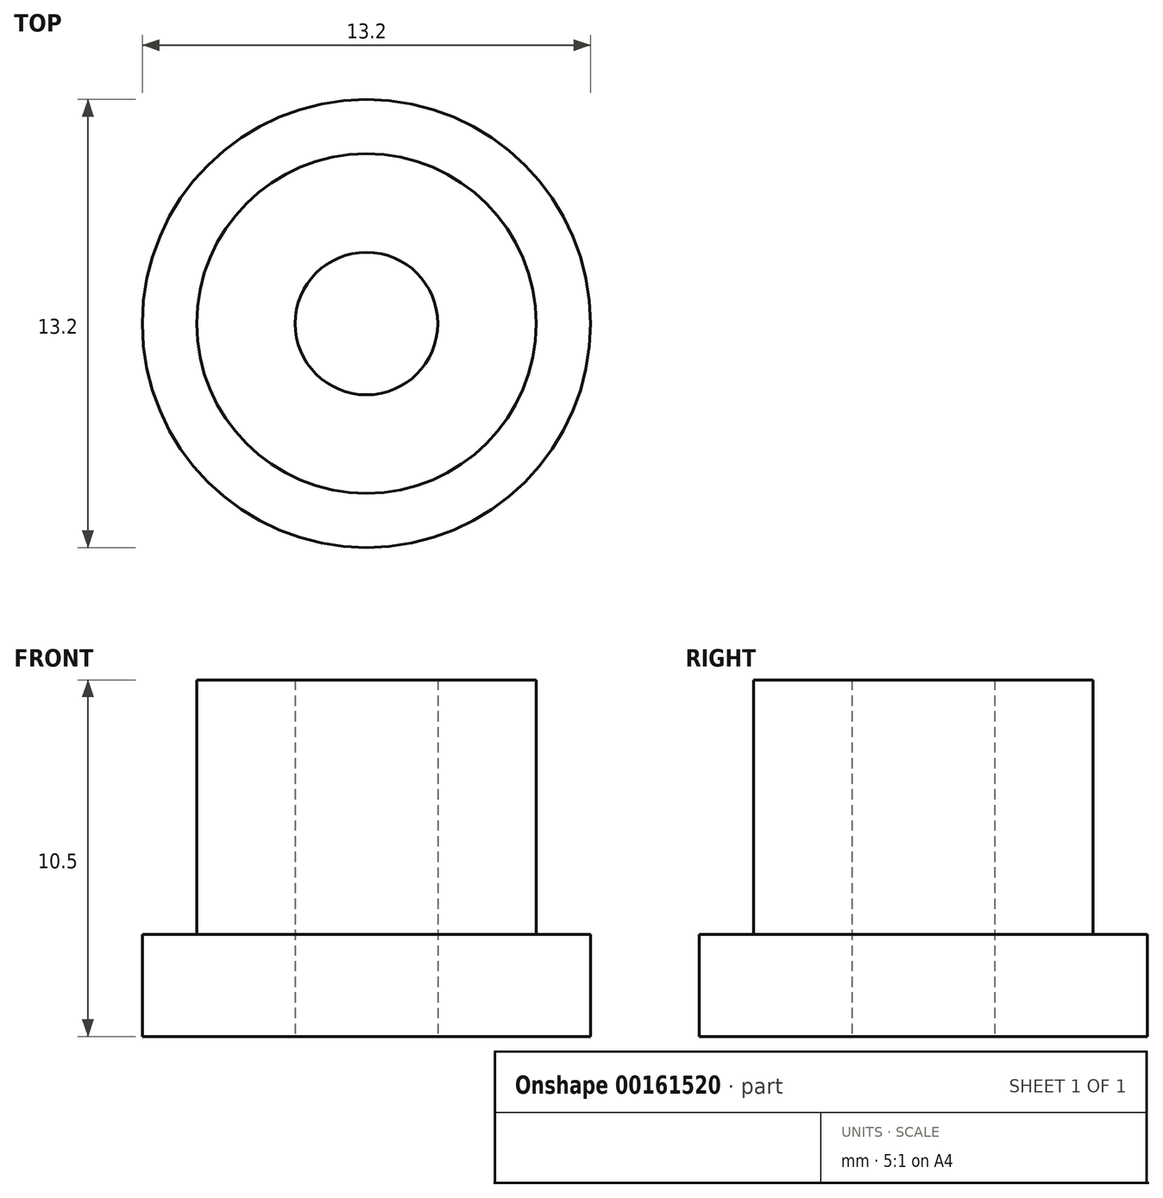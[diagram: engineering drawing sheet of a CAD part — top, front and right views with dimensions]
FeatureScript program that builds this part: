
annotation { "Feature Type Name" : "Feature", "Feature Type Description" : "" }
export const myFeature = defineFeature(function(context is Context, id is Id, definition is map)
    precondition{}
    {
        {
            var Q0;
            Q0=qCreatedBy(makeId("Top.planeOp"),FACE);
            var sketch = newSketch(context, id + "F0", { "sketchPlane" : qUnion([Q0])});
            skCircle(sketch, "E0", {"center": v(0, 0) * mm, "radius": 6.6 * mm});
            skCircle(sketch, "E1", {"center": v(0, 0) * mm, "radius": 2.1 * mm});
            skSolve(sketch);
        }
        {
            var Q0;
            Q0=makeQuery(id+"F0.imprint","IMPRINT",FACE,{"disambiguationData":[TD([[makeQuery(id+"F0.imprint","IMPRINT",EDGE,{"derivedFrom":sQuery(id+"F0.wireOp",EDGE,"E0")}),1.0]])]});
            extrude(context, id + "F1", {"entities" : qUnion([Q0]), "depth" : 3 * mm});
        }
        {
            var Q0;
            Q0=makeQuery(id+"F1.opExtrude","CAP_FACE",FACE,{"disambiguationData":[OSD([sQuery(id+"F0.wireOp",EDGE,"E0"),sQuery(id+"F0.wireOp",EDGE,"E1")])],"isStart":false});
            var sketch = newSketch(context, id + "F2", { "sketchPlane" : qUnion([Q0])});
            skCircle(sketch, "E2", {"center": v(0, 0) * mm, "radius": 5 * mm});
            skCircle(sketch, "E3", {"center": v(0, 0) * mm, "radius": 2.1 * mm});
            skSolve(sketch);
        }
        {
            var Q0;
            Q0=makeQuery(id+"F2.imprint","IMPRINT",FACE,{"disambiguationData":[TD([[makeQuery(id+"F2.imprint","IMPRINT",EDGE,{"derivedFrom":sQuery(id+"F2.wireOp",EDGE,"E2")}),1.0]])]});
            extrude(context, id + "F3", {"entities" : qUnion([Q0]), "operationType" : NewBodyOperationType.ADD, "depth" : 7.5 * mm});
        }
    });
